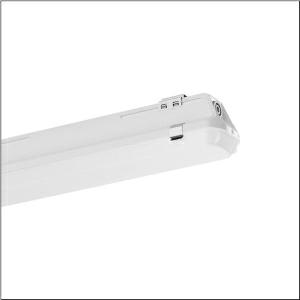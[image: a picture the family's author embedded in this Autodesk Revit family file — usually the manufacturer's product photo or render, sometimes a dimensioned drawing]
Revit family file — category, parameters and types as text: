
# Revit family: monsun_r__11_emergency_51fp10dp460hr_ed92
name_source: partatom
category: Lighting Fixtures
units: mm (PartAtom-declared; Revit-internal decimal feet)

## family parameters
Cut with Voids When Loaded = No
Host = Face
Light Source = No
Part Type = Normal
Room Calculation Point = No
Round Connector Dimension = Use Diameter
Shared = No

## types (1)
- --- (1 x LED, 890 lm, 6.9 W, 4000K)
    Apparent Load = 7 VA
    CIE Flux Codes = 47 77 93 94 100
    Color Rendering = 80
    Color Temperature = 4000K
    Default Elevation = 1800 mm
    Description = Monsun® 11 emergency, damp-proof luminaire, chain hanger, primary optical cover: enclosure, of PMMA, light emission: direct distribution, primary light characteristic: symmetric, installation type: suspended mounting, surface-mounted, horizontal mounting, vertical mounting, LED, rated luminous flux: 6.050lm, luminous efficacy: 175lm/W, light colour: 840, colour temperature: 4000K, control gear: ECG DALI, with terminal, 5+2-pole, max. 2.5mm², mains connection: 220..240V, AC/DC, 0/50..60Hz, rated input power: 35W, changeover relay for equivalent power supply, AC/DC, 0/50..60Hz, luminaire housing, of glass-fibre reinforced polyester, uncoated, bright grey, incl. chain hanger, length: 1.590mm, width: 90mm, height: 88mm, clip for enclosure, of stainless steel (V2A), ceiling mounting element, of stainless steel (V2A), chain hanger, of stainless steel (V2A), protection rating (complete): IP66, insulation class (complete): insulation class I (protective earthing), certification: CE, UKCA, protection symbol: D, impact resistance: IK04, permissible operating ambient temperature: -25..+35°C, standard: EN 50419, EN 60598-2-1, EN 60598-2-22, no direct snow, no direct sun, no direct rain, for indoor or canopied outdoor use, corresponds to IFS (International Featured Standards) requirements for safety and quality in the food industry, contact your sales advisor before using the luminaires in applications with unclear chemical exposure, large temperature fluctuations or condensation-forming humidity, LABS conformity tested according to VDMA 24364:2018-05, packaging unit: 1 piece
    Height = 89 mm
    Lamp = 1 x LED
    Lamp Light Flux = 890 lm
    Lamp Power = 6.9 W
    Lamp count = 1
    Length = 1590 mm
    Luminous efficacy = 129 lm/W
    Manufacturer = Siteco
    ModVariant = No
    Model = 51FP10DP460HR
    Mounting Place = Ceiling
    Mounting Type = Surface mounted
    Number of Poles = 1
    OnlyDefault = Yes
    Power Factor = 1
    Product Name = Monsun® 11 emergency
    Product group = damp-proof luminaire
    ProductGroupID = 300
    Protection Class = Protection class I
    Protection Degree = IP 66
    RLX_Detail_Level = 1
    RLX_Emergency_Light_Flux = 0 lm
    RLX_Emergency_Type = 0
    RLX_Emergency_Type_DB = No
    RlxData = <blob elided: 93289 chars, md5=bd5f22b0>
    Socket = socket
    Standby Power = 0 W
    System Light Flux = 890 lm
    System Power = 7 W
    Type Comments = : equivalent power supply (DC)
    Type Image = l_1004748.jpg
    URL = http://relux.com
    VarID = @adj_134667
    Voltage = 0 V
    Weight = 0.00 kg
    Width = 90 mm

## geometry (parser evidence)
native form markers: Blend x4, Sweep x14
no freeform markers — native parametric forms only
